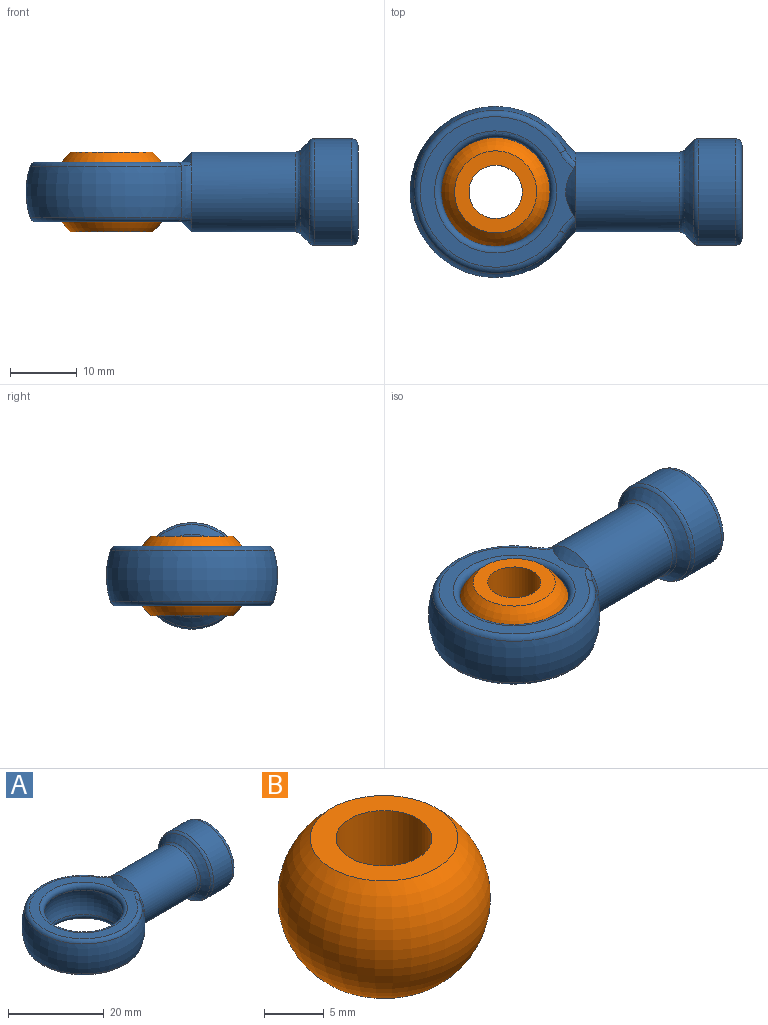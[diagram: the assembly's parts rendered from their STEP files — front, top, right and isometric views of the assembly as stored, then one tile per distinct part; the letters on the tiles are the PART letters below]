
ASSEMBLY  parts=2 mates=1
PART A: 25 faces, bbox 50.3x26.6x17.3 mm
  f0: cone r=4.5mm half-angle=45deg, axis (1,0,0), area 11.7mm2, adj f3,f9,f14,f16
  f1: plane 23.05x22.61mm, normal (0,0,1), area 137.6mm2, adj f5,f17,f18,f19,f23
  f2: torus R=0.88mm, axis (0,0,1), area 347.9mm2, adj f23,f24
  f3: plane 23.05x22.61mm, normal (0,0,-1), area 137.6mm2, adj f0,f14,f15,f16,f24
  f4: torus R=0.88mm, axis (0,0,1), area 502.7mm2, adj f10,f11,f15,f18
  f5: cone r=4.5mm half-angle=45deg, axis (1,0,0), area 11.7mm2, adj f1,f9,f17,f19
  f6: plane 14x14mm, normal (1,0,0), area 58.9mm2, adj f13,f20
  f7: cylinder r=8mm len=16mm, axis (-1,0,0), area 280.8mm2, adj f20,f21
  f8: cone r=6mm half-angle=45deg, axis (1,0,0), area 88mm2, adj f21,f22
  f9: cylinder r=6mm len=15.59mm, axis (-1,0,0), area 587.6mm2, adj f0,f5,f10,f11,f22
  f10: bspline ~9.95x2.98mm, area 17.3mm2, adj f4,f9,f16,f19
  f11: bspline ~9.95x2.98mm, area 17.3mm2, adj f4,f9,f14,f17
  f12: cone r=0mm half-angle=59deg, axis (1,0,0), area 110.9mm2, adj f13
  f13: cylinder r=5.5mm len=20mm, axis (1,0,0), area 691.2mm2, adj f6,f12
  f14: bspline ~4.36x3.59mm, area 3mm2, adj f0,f3,f11,f15
  f15: torus R=11.3mm, axis (0,0,1), area 76.8mm2, adj f3,f4,f14,f16
  f16: bspline ~4.35x3.56mm, area 3mm2, adj f0,f3,f10,f15
  f17: bspline ~4.36x3.59mm, area 3mm2, adj f1,f5,f11,f18
  f18: torus R=11.3mm, axis (0,0,1), area 76.8mm2, adj f1,f4,f17,f19
  f19: bspline ~4.35x3.56mm, area 3mm2, adj f1,f5,f10,f18
  f20: torus R=7mm, axis (1,0,0), area 75.4mm2, adj f6,f7
  f21: torus R=7mm, axis (1,0,0), area 39mm2, adj f7,f8
  f22: torus R=7mm, axis (-1,0,0), area 30.1mm2, adj f8,f9
  f23: torus R=9.17mm, axis (0,0,1), area 104.8mm2, adj f1,f2
  f24: torus R=9.17mm, axis (0,0,1), area 104.8mm2, adj f2,f3
PART B: 4 faces, bbox 17.8x17.8x12 mm
  f0: torus R=0.88mm, axis (0,0,1), area 677.8mm2, adj f1,f3
  f1: plane 12.33x12.33mm, normal (0,0,1), area 69.2mm2, adj f0,f2
  f2: cylinder r=4mm len=12mm, axis (0,0,1), area 301.6mm2, adj f1,f3
  f3: plane 12.33x12.33mm, normal (0,0,-1), area 69.2mm2, adj f0,f2
PLACE A t=(-1.76,35.85,7.56)mm
PLACE B t=(-1.76,35.85,7.56)mm
MATE ball A.f2 <-> B.f0  axis (0,0,1) through (-1.76,35.85,7.56)mm
